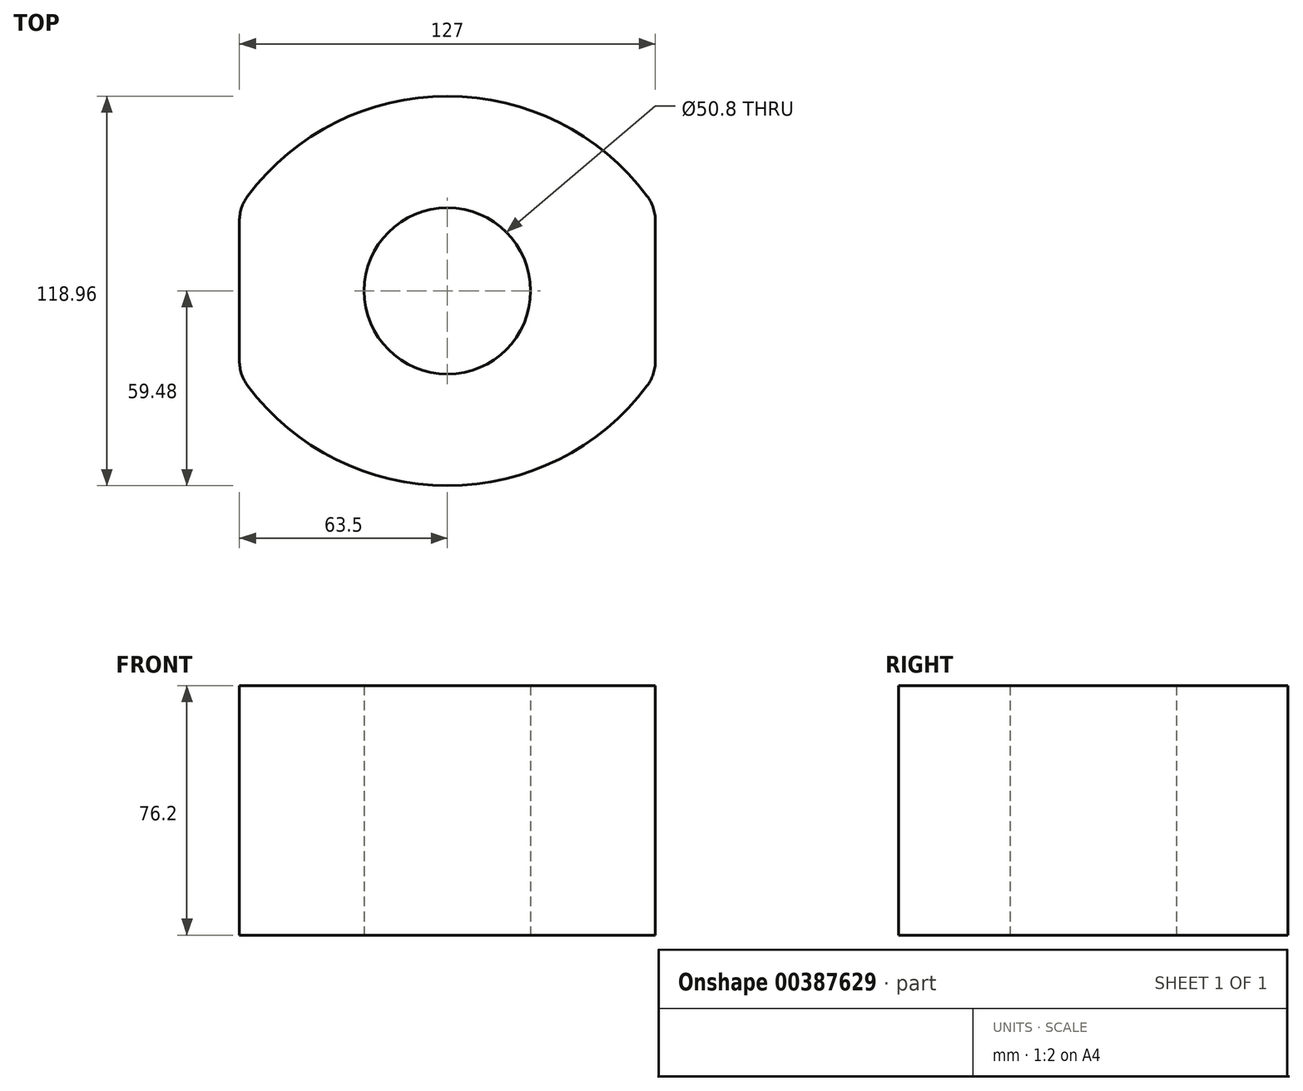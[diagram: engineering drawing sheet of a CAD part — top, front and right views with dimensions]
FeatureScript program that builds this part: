
annotation { "Feature Type Name" : "Feature", "Feature Type Description" : "" }
export const myFeature = defineFeature(function(context is Context, id is Id, definition is map)
    precondition{}
    {
        {
            var Q0;
            Q0=qCreatedBy(makeId("Top.planeOp"),FACE);
            var sketch = newSketch(context, id + "F0", { "sketchPlane" : qUnion([Q0])});
            skLineSegment(sketch, "E0.bottom", {"start": v(63.5, 25.4) * mm, "end": v(-63.5, 25.4) * mm});
            skLineSegment(sketch, "E0.top", {"start": v(63.5, -25.4) * mm, "end": v(-63.5, -25.4) * mm});
            skLineSegment(sketch, "E0.left", {"start": v(63.5, 25.4) * mm, "end": v(63.5, -25.4) * mm});
            skLineSegment(sketch, "E0.right", {"start": v(-63.5, 25.4) * mm, "end": v(-63.5, -25.4) * mm});
            skPoint(sketch, "E0.middle", {"position": v(0, 0) * mm});
            skCircle(sketch, "E1", {"center": v(0, 0) * mm, "radius": 25.4 * mm});
            skArc(sketch, "E2", {"start": v(63.5, 25.4) * mm, "mid": v(0, 59.48) * mm, "end": v(-63.5, 25.4) * mm});
            skArc(sketch, "E3", {"start": v(-63.5, -25.4) * mm, "mid": v(0, -59.48) * mm, "end": v(63.5, -25.4) * mm});
            skSolve(sketch);
        }
        {
            var Q0;
            {var subQ0=sQuery(id+"F0.wireOp",EDGE,"E2");Q0=makeQuery(id+"F0.imprint","IMPRINT",FACE,{"disambiguationData":[TD([[makeQuery(id+"F0.imprint","IMPRINT",EDGE,{"derivedFrom":subQ0}),1.0]])]});}
            var Q1;
            {var subQ0=sQuery(id+"F0.wireOp",EDGE,"E0.right");Q1=makeQuery(id+"F0.imprint","IMPRINT",FACE,{"disambiguationData":[TD([[makeQuery(id+"F0.imprint","IMPRINT",EDGE,{"derivedFrom":subQ0}),1.0]])]});}
            var Q2;
            {var subQ0=sQuery(id+"F0.wireOp",EDGE,"E0.left");Q2=makeQuery(id+"F0.imprint","IMPRINT",FACE,{"disambiguationData":[TD([[makeQuery(id+"F0.imprint","IMPRINT",EDGE,{"derivedFrom":subQ0}),-1.0]])]});}
            var Q3;
            {var subQ0=sQuery(id+"F0.wireOp",EDGE,"E3");Q3=makeQuery(id+"F0.imprint","IMPRINT",FACE,{"disambiguationData":[TD([[makeQuery(id+"F0.imprint","IMPRINT",EDGE,{"derivedFrom":subQ0}),1.0]])]});}
            extrude(context, id + "F1", {"entities" : qUnion([Q0, Q1, Q2, Q3]), "endBound" : BoundingType.SYMMETRIC, "depth" : 76.2 * mm});
        }
        {
            var Q0;
            Q0=makeQuery(id+"F1.opExtrude","SWEPT_EDGE",EDGE,{"disambiguationData":[OSD([sQuery(id+"F0.wireOp",EDGE,"E0.bottom"),sQuery(id+"F0.wireOp",EDGE,"E0.right"),sQuery(id+"F0.wireOp",EDGE,"E2")])]});
            var Q1;
            Q1=makeQuery(id+"F1.opExtrude","SWEPT_EDGE",EDGE,{"disambiguationData":[OSD([sQuery(id+"F0.wireOp",EDGE,"E0.top"),sQuery(id+"F0.wireOp",EDGE,"E0.right"),sQuery(id+"F0.wireOp",EDGE,"E3")])]});
            var Q2;
            Q2=makeQuery(id+"F1.opExtrude","SWEPT_EDGE",EDGE,{"disambiguationData":[OSD([sQuery(id+"F0.wireOp",EDGE,"E0.bottom"),sQuery(id+"F0.wireOp",EDGE,"E0.left"),sQuery(id+"F0.wireOp",EDGE,"E2")])]});
            var Q3;
            Q3=makeQuery(id+"F1.opExtrude","SWEPT_EDGE",EDGE,{"disambiguationData":[OSD([sQuery(id+"F0.wireOp",EDGE,"E0.top"),sQuery(id+"F0.wireOp",EDGE,"E0.left"),sQuery(id+"F0.wireOp",EDGE,"E3")])]});
            fillet(context, id + "F2", {"entities" : qUnion([Q0, Q1, Q2, Q3]), "radius" : 12.7 * mm, "tangentPropagation" : true, "allowEdgeOverflow" : false});
        }
    });
